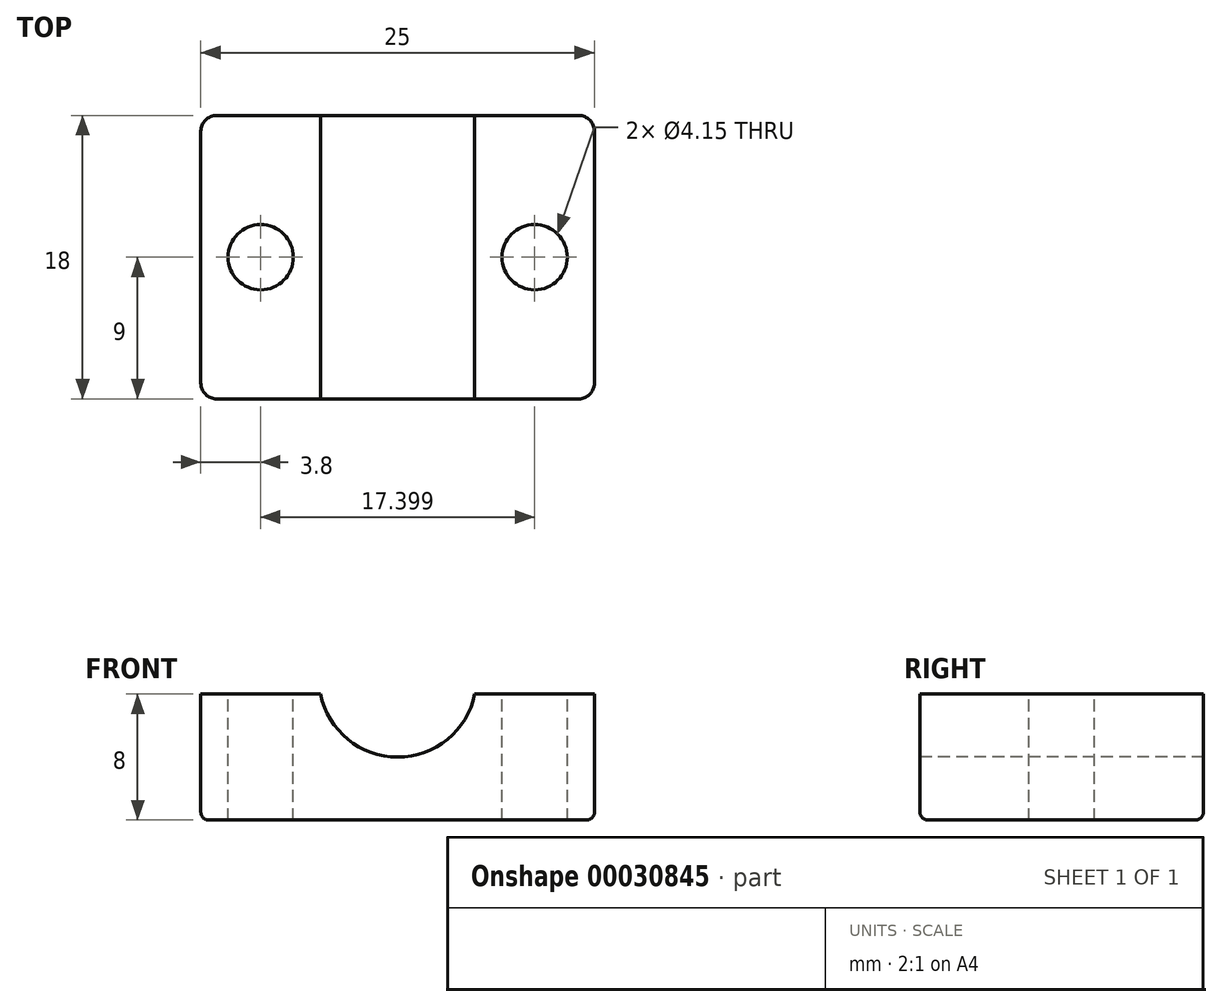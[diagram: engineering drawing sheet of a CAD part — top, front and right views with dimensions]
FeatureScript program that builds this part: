
annotation { "Feature Type Name" : "Feature", "Feature Type Description" : "" }
export const myFeature = defineFeature(function(context is Context, id is Id, definition is map)
    precondition{}
    {
        {
            var Q0;
            Q0=qCreatedBy(makeId("Top.planeOp"),FACE);
            var sketch = newSketch(context, id + "F0", { "sketchPlane" : qUnion([Q0])});
            skLineSegment(sketch, "E0.rect.bottom", {"start": v(12.5, -9) * mm, "end": v(-12.5, -9) * mm});
            skLineSegment(sketch, "E0.rect.top", {"start": v(12.5, 9) * mm, "end": v(-12.5, 9) * mm});
            skLineSegment(sketch, "E0.rect.left", {"start": v(12.5, -9) * mm, "end": v(12.5, 9) * mm});
            skLineSegment(sketch, "E0.rect.right", {"start": v(-12.5, -9) * mm, "end": v(-12.5, 9) * mm});
            skPoint(sketch, "E0.rect.middle", {"position": v(0, 0) * mm});
            skSolve(sketch);
        }
        {
            var Q0;
            Q0=makeQuery(id+"F0.imprint","IMPRINT",FACE,{"disambiguationData":[TD([[makeQuery(id+"F0.imprint","IMPRINT",EDGE,{"derivedFrom":sQuery(id+"F0.wireOp",EDGE,"E0.rect.bottom")}),-1.0]])]});
            extrude(context, id + "F1", {"entities" : qUnion([Q0]), "depth" : 8 * mm});
        }
        {
            var Q0;
            Q0=makeQuery(id+"F1.opExtrude","SWEPT_FACE",FACE,{"disambiguationData":[OSD([sQuery(id+"F0.wireOp",EDGE,"E0.rect.bottom")])]});
            var sketch = newSketch(context, id + "F2", { "sketchPlane" : qUnion([Q0])});
            skLineSegment(sketch, "E1", {"start": v(0, 0) * mm, "end": v(0, 8) * mm, "construction": true});
            skLineSegment(sketch, "E2", {"start": v(0, 8) * mm, "end": v(0, 9) * mm, "construction": true});
            skCircle(sketch, "E3", {"center": v(0, 9) * mm, "radius": 5 * mm});
            skSolve(sketch);
        }
        {
            var Q0;
            {var subQ0=makeQuery(id+"F1.opExtrude","CAP_EDGE",EDGE,{"disambiguationData":[OSD([sQuery(id+"F0.wireOp",EDGE,"E0.rect.bottom")])],"isStart":false});var subQ1=sQuery(id+"F2.wireOp",EDGE,"E3");var subQ3=makeQuery(id+"F2.imprint","INTERSECT",VERTEX,{"disambiguationData":[OD(0.0)],"derivedFrom":[subQ0,subQ1]});Q0=makeQuery(id+"F2.imprint","IMPRINT",FACE,{"disambiguationData":[TD([[makeQuery(id+"F2.imprint","IMPRINT",EDGE,{"disambiguationData":[TD([[subQ3,1.0]])],"derivedFrom":subQ1}),1.0]])]});}
            extrude(context, id + "F3", {"entities" : qUnion([Q0]), "operationType" : NewBodyOperationType.REMOVE, "oppositeDirection" : true, "depth" : 25 * mm});
        }
        {
            var Q0;
            {var subQ0=sQuery(id+"F0.wireOp",EDGE,"E0.rect.bottom");var subQ1=sQuery(id+"F0.wireOp",EDGE,"E0.rect.top");var subQ2=sQuery(id+"F0.wireOp",EDGE,"E0.rect.right");Q0=makeQuery(id+"F3.boolean.opBoolean","SPLIT",FACE,{"disambiguationData":[TD([makeQuery(id+"F1.opExtrude","SWEPT_FACE",FACE,{"disambiguationData":[OSD([subQ2])]})])],"derivedFrom":makeQuery(id+"F1.opExtrude","CAP_FACE",FACE,{"disambiguationData":[OSD([subQ0,subQ1,sQuery(id+"F0.wireOp",EDGE,"E0.rect.left"),subQ2])],"isStart":false})});}
            var sketch = newSketch(context, id + "F4", { "sketchPlane" : qUnion([Q0])});
            skLineSegment(sketch, "E4", {"start": v(-12.5, 0) * mm, "end": v(-4.9, 0) * mm, "construction": true});
            skCircle(sketch, "E5", {"center": v(-8.7, 0) * mm, "radius": 2.08 * mm});
            skSolve(sketch);
        }
        {
            var Q0;
            {var subQ0=sQuery(id+"F0.wireOp",EDGE,"E0.rect.bottom");var subQ1=sQuery(id+"F0.wireOp",EDGE,"E0.rect.top");var subQ2=sQuery(id+"F0.wireOp",EDGE,"E0.rect.left");Q0=makeQuery(id+"F3.boolean.opBoolean","SPLIT",FACE,{"disambiguationData":[TD([makeQuery(id+"F1.opExtrude","SWEPT_FACE",FACE,{"disambiguationData":[OSD([subQ2])]})])],"derivedFrom":makeQuery(id+"F1.opExtrude","CAP_FACE",FACE,{"disambiguationData":[OSD([subQ0,subQ1,subQ2,sQuery(id+"F0.wireOp",EDGE,"E0.rect.right")])],"isStart":false})});}
            var sketch = newSketch(context, id + "F5", { "sketchPlane" : qUnion([Q0])});
            skLineSegment(sketch, "E6", {"start": v(12.5, 0) * mm, "end": v(4.9, 0) * mm, "construction": true});
            skCircle(sketch, "E7", {"center": v(8.7, 0) * mm, "radius": 2.08 * mm});
            skSolve(sketch);
        }
        {
            var Q0;
            Q0=makeQuery(id+"F4.imprint","IMPRINT",FACE,{"disambiguationData":[TD([[makeQuery(id+"F4.imprint","IMPRINT",EDGE,{"derivedFrom":sQuery(id+"F4.wireOp",EDGE,"E5")}),1.0]])]});
            var Q1;
            Q1=makeQuery(id+"F5.imprint","IMPRINT",FACE,{"disambiguationData":[TD([[makeQuery(id+"F5.imprint","IMPRINT",EDGE,{"derivedFrom":sQuery(id+"F5.wireOp",EDGE,"E7")}),1.0]])]});
            extrude(context, id + "F6", {"entities" : qUnion([Q0, Q1]), "operationType" : NewBodyOperationType.REMOVE, "oppositeDirection" : true, "depth" : 25 * mm});
        }
        {
            var Q0;
            Q0=makeQuery(id+"F1.opExtrude","SWEPT_EDGE",EDGE,{"disambiguationData":[OSD([sQuery(id+"F0.wireOp",EDGE,"E0.rect.bottom"),sQuery(id+"F0.wireOp",EDGE,"E0.rect.right")])]});
            var Q1;
            Q1=makeQuery(id+"F1.opExtrude","SWEPT_EDGE",EDGE,{"disambiguationData":[OSD([sQuery(id+"F0.wireOp",EDGE,"E0.rect.bottom"),sQuery(id+"F0.wireOp",EDGE,"E0.rect.left")])]});
            var Q2;
            Q2=makeQuery(id+"F1.opExtrude","SWEPT_EDGE",EDGE,{"disambiguationData":[OSD([sQuery(id+"F0.wireOp",EDGE,"E0.rect.top"),sQuery(id+"F0.wireOp",EDGE,"E0.rect.left")])]});
            var Q3;
            Q3=makeQuery(id+"F1.opExtrude","SWEPT_EDGE",EDGE,{"disambiguationData":[OSD([sQuery(id+"F0.wireOp",EDGE,"E0.rect.top"),sQuery(id+"F0.wireOp",EDGE,"E0.rect.right")])]});
            fillet(context, id + "F7", {"entities" : qUnion([Q0, Q1, Q2, Q3]), "radius" : 1 * mm, "tangentPropagation" : true, "allowEdgeOverflow" : false});
        }
        {
            var Q0;
            Q0=makeQuery(id+"F1.opExtrude","CAP_EDGE",EDGE,{"disambiguationData":[OSD([sQuery(id+"F0.wireOp",EDGE,"E0.rect.right")])],"isStart":true});
            fillet(context, id + "F8", {"entities" : qUnion([Q0]), "radius" : .5 * mm, "tangentPropagation" : true, "allowEdgeOverflow" : false});
        }
    });
